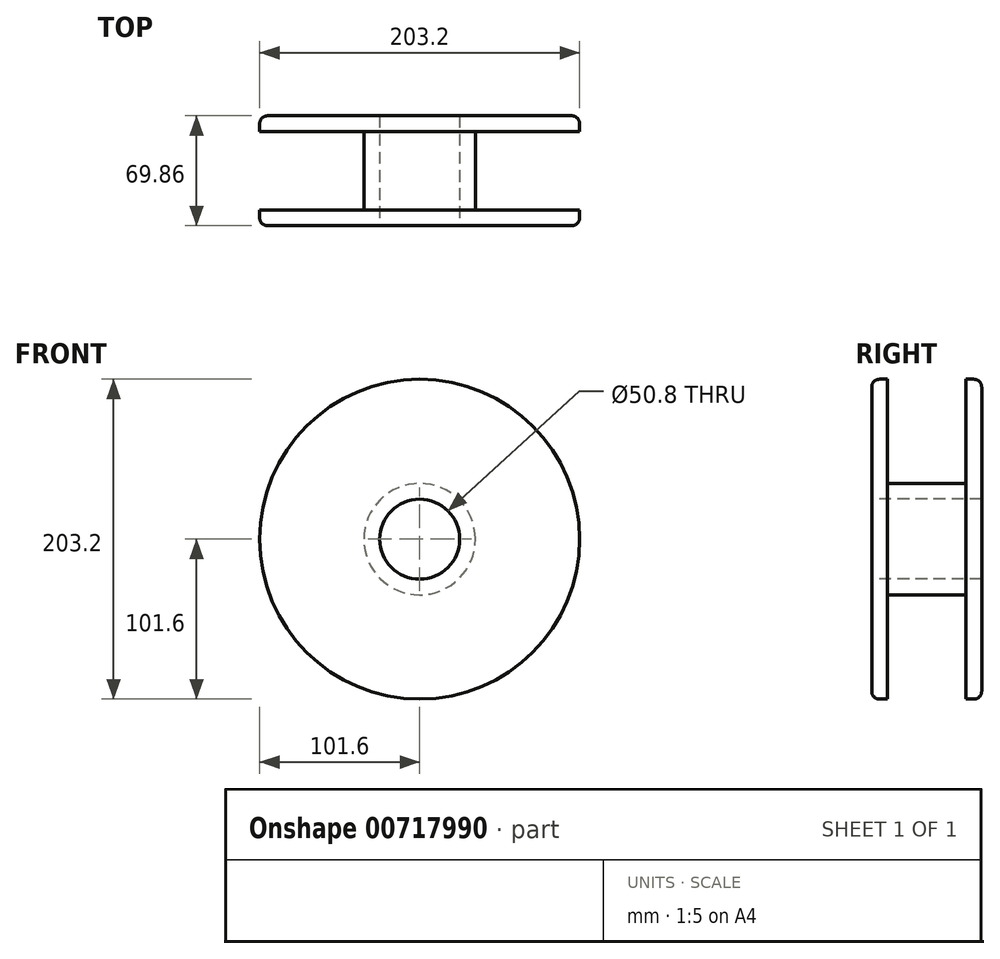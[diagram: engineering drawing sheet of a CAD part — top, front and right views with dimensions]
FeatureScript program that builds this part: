
annotation { "Feature Type Name" : "Feature", "Feature Type Description" : "" }
export const myFeature = defineFeature(function(context is Context, id is Id, definition is map)
    precondition{}
    {
        {
            var Q0;
            Q0=qCreatedBy(makeId("Top.planeOp"),FACE);
            var sketch = newSketch(context, id + "F0", { "sketchPlane" : qUnion([Q0])});
            skLineSegment(sketch, "E0", {"start": v(0, 0) * mm, "end": v(0, -34.93) * mm});
            skLineSegment(sketch, "E1", {"start": v(0, 0) * mm, "end": v(0, 34.93) * mm});
            skLineSegment(sketch, "E2", {"start": v(0, 34.93) * mm, "end": v(25.4, 34.93) * mm});
            skLineSegment(sketch, "E3", {"start": v(25.4, 34.93) * mm, "end": v(25.4, -34.93) * mm});
            skLineSegment(sketch, "E4", {"start": v(25.4, -34.93) * mm, "end": v(0, -34.93) * mm});
            skLineSegment(sketch, "E5.bottom", {"start": v(25.4, 34.93) * mm, "end": v(101.6, 34.93) * mm});
            skLineSegment(sketch, "E5.top", {"start": v(25.4, 24.93) * mm, "end": v(101.6, 24.93) * mm});
            skLineSegment(sketch, "E5.left", {"start": v(25.4, 34.93) * mm, "end": v(25.4, 24.93) * mm});
            skLineSegment(sketch, "E5.right", {"start": v(101.6, 34.93) * mm, "end": v(101.6, 24.93) * mm});
            skLineSegment(sketch, "E6.bottom", {"start": v(25.4, -34.93) * mm, "end": v(101.6, -34.93) * mm});
            skLineSegment(sketch, "E6.top", {"start": v(25.4, -24.92) * mm, "end": v(101.6, -24.92) * mm});
            skLineSegment(sketch, "E6.left", {"start": v(25.4, -34.93) * mm, "end": v(25.4, -24.92) * mm});
            skLineSegment(sketch, "E6.right", {"start": v(101.6, -34.93) * mm, "end": v(101.6, -24.92) * mm});
            skLineSegment(sketch, "E7", {"start": v(25.4, -24.92) * mm, "end": v(35.4, -24.92) * mm});
            skLineSegment(sketch, "E8", {"start": v(25.4, -24.92) * mm, "end": v(25.4, -14.92) * mm});
            skLineSegment(sketch, "E9", {"start": v(25.4, 24.93) * mm, "end": v(25.4, 14.93) * mm});
            skLineSegment(sketch, "E10", {"start": v(25.4, 24.93) * mm, "end": v(35.4, 24.93) * mm});
            skLineSegment(sketch, "E11", {"start": v(35.4, 24.93) * mm, "end": v(35.4, -24.92) * mm});
            skLineSegment(sketch, "E12", {"start": v(35.4, -24.92) * mm, "end": v(45.4, -24.92) * mm});
            skLineSegment(sketch, "E13", {"start": v(35.4, 24.93) * mm, "end": v(45.4, 24.93) * mm});
            skArc(sketch, "E14", {"start": v(45.4, 24.93) * mm, "mid": v(38.33, 22) * mm, "end": v(35.4, 14.93) * mm});
            skArc(sketch, "E15", {"start": v(35.4, -14.92) * mm, "mid": v(38.33, -22) * mm, "end": v(45.4, -24.92) * mm});
            skSolve(sketch);
        }
        {
            var Q0;
            Q0=makeQuery(id+"F0.imprint","IMPRINT",FACE,{"disambiguationData":[TD([[makeQuery(id+"F0.imprint","IMPRINT",EDGE,{"derivedFrom":sQuery(id+"F0.wireOp",EDGE,"E3")}),1.0]])]});
            var Q1;
            {var subQ0=sQuery(id+"F0.wireOp",EDGE,"E13");Q1=makeQuery(id+"F0.imprint","IMPRINT",FACE,{"disambiguationData":[TD([[makeQuery(id+"F0.imprint","IMPRINT",EDGE,{"derivedFrom":subQ0}),-1.0]])]});}
            var Q2;
            Q2=makeQuery(id+"F0.imprint","IMPRINT",FACE,{"disambiguationData":[TD([[makeQuery(id+"F0.imprint","IMPRINT",EDGE,{"derivedFrom":sQuery(id+"F0.wireOp",EDGE,"E5.bottom")}),-1.0]])]});
            var Q3;
            Q3=makeQuery(id+"F0.imprint","IMPRINT",FACE,{"disambiguationData":[TD([[makeQuery(id+"F0.imprint","IMPRINT",EDGE,{"derivedFrom":sQuery(id+"F0.wireOp",EDGE,"E6.bottom")}),1.0]])]});
            var Q4;
            {var subQ0=sQuery(id+"F0.wireOp",EDGE,"E12");Q4=makeQuery(id+"F0.imprint","IMPRINT",FACE,{"disambiguationData":[TD([[makeQuery(id+"F0.imprint","IMPRINT",EDGE,{"derivedFrom":subQ0}),1.0]])]});}
            var Q5;
            Q5=sQuery(id+"F0.wireOp",EDGE,"E1");
            revolve(context, id + "F1", {"surfaceOperationType" : NewSurfaceOperationType.NEW, "entities" : qUnion([Q0, Q1, Q2, Q3, Q4]), "axis" : qUnion([Q5]), "revolveType" : RevolveType.FULL});
        }
        {
            var Q0;
            Q0=makeQuery(id+"F1.opRevolve","SWEPT_EDGE",EDGE,{"disambiguationData":[OSD([sQuery(id+"F0.wireOp",EDGE,"E5.bottom"),sQuery(id+"F0.wireOp",EDGE,"E5.right")])]});
            var Q1;
            Q1=makeQuery(id+"F1.opRevolve","SWEPT_EDGE",EDGE,{"disambiguationData":[OSD([sQuery(id+"F0.wireOp",EDGE,"E6.bottom"),sQuery(id+"F0.wireOp",EDGE,"E6.right")])]});
            fillet(context, id + "F2", {"entities" : qUnion([Q0, Q1]), "radius" : 5 * mm, "tangentPropagation" : true, "allowEdgeOverflow" : false});
        }
    });
